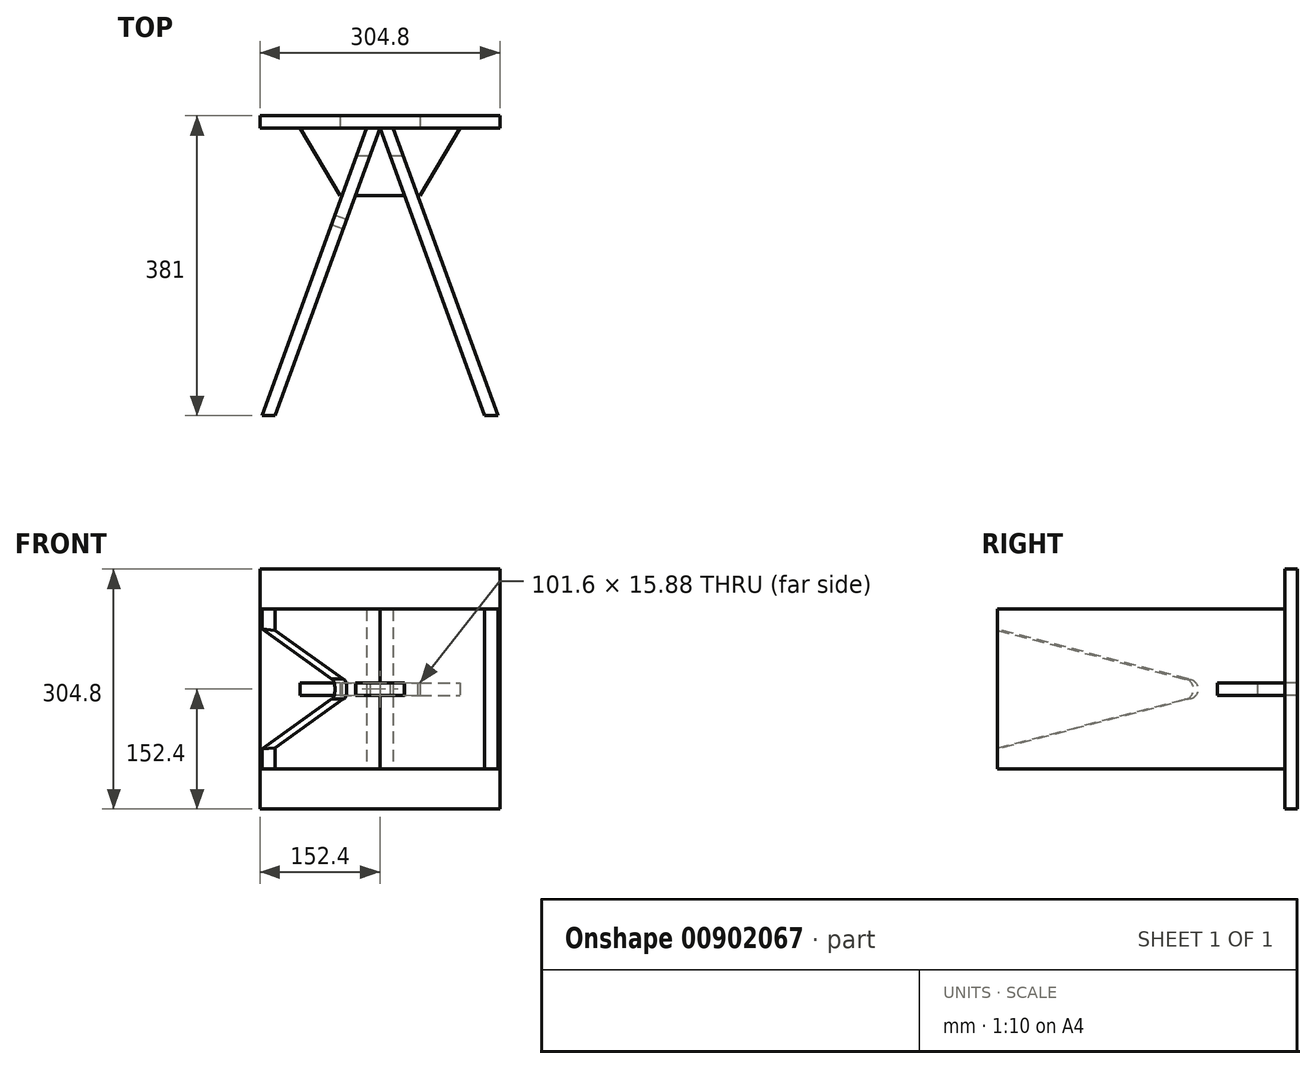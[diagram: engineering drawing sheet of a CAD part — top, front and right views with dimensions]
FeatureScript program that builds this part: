
annotation { "Feature Type Name" : "Feature", "Feature Type Description" : "" }
export const myFeature = defineFeature(function(context is Context, id is Id, definition is map)
    precondition{}
    {
        {
            var Q0;
            Q0=qCreatedBy(makeId("Front.planeOp"),FACE);
            var sketch = newSketch(context, id + "F0", { "sketchPlane" : qUnion([Q0])});
            skLineSegment(sketch, "E0.bottom", {"start": v(152.4, 152.4) * mm, "end": v(-152.4, 152.4) * mm});
            skLineSegment(sketch, "E0.top", {"start": v(152.4, -152.4) * mm, "end": v(-152.4, -152.4) * mm});
            skLineSegment(sketch, "E0.left", {"start": v(152.4, 152.4) * mm, "end": v(152.4, -152.4) * mm});
            skLineSegment(sketch, "E0.right", {"start": v(-152.4, 152.4) * mm, "end": v(-152.4, -152.4) * mm});
            skPoint(sketch, "E0.middle", {"position": v(0, 0) * mm});
            skLineSegment(sketch, "E1.bottom", {"start": v(50.8, 7.94) * mm, "end": v(-50.8, 7.94) * mm});
            skLineSegment(sketch, "E1.top", {"start": v(50.8, -7.94) * mm, "end": v(-50.8, -7.94) * mm});
            skLineSegment(sketch, "E1.left", {"start": v(50.8, 7.94) * mm, "end": v(50.8, -7.94) * mm});
            skLineSegment(sketch, "E1.right", {"start": v(-50.8, 7.94) * mm, "end": v(-50.8, -7.94) * mm});
            skSolve(sketch);
        }
        {
            var Q0;
            Q0=makeQuery(id+"F0.imprint","IMPRINT",FACE,{"disambiguationData":[TD([[makeQuery(id+"F0.imprint","IMPRINT",EDGE,{"derivedFrom":sQuery(id+"F0.wireOp",EDGE,"E0.bottom")}),1.0]])]});
            extrude(context, id + "F1", {"entities" : qUnion([Q0]), "depth" : 15.88 * mm, "offsetDistance" : 25.4 * mm});
        }
        {
            var Q0;
            Q0=qCreatedBy(makeId("Top.planeOp"),FACE);
            var sketch = newSketch(context, id + "F2", { "sketchPlane" : qUnion([Q0])});
            skLineSegment(sketch, "E2.bottom", {"start": v(-50.8, 0) * mm, "end": v(50.8, 0) * mm});
            skLineSegment(sketch, "E2.top", {"start": v(-50.8, -101.6) * mm, "end": v(50.8, -101.6) * mm});
            skLineSegment(sketch, "E2.left", {"start": v(-50.8, 0) * mm, "end": v(-50.8, -101.6) * mm});
            skLineSegment(sketch, "E2.right", {"start": v(50.8, 0) * mm, "end": v(50.8, -101.6) * mm});
            skLineSegment(sketch, "E3.bottom", {"start": v(-50.8, -15.88) * mm, "end": v(-101.6, -15.88) * mm});
            skLineSegment(sketch, "E3.left", {"start": v(-50.8, -15.88) * mm, "end": v(-50.8, -127) * mm});
            skLineSegment(sketch, "E4.bottom", {"start": v(50.8, -15.88) * mm, "end": v(101.6, -15.87) * mm});
            skLineSegment(sketch, "E4.left", {"start": v(50.8, -15.88) * mm, "end": v(50.8, -127) * mm});
            skPoint(sketch, "E5", {"position": v(0, 0) * mm});
            skPoint(sketch, "E6", {"position": v(0, -15.88) * mm});
            skLineSegment(sketch, "E7", {"start": v(0, -15.88) * mm, "end": v(-132.9, -381) * mm});
            skLineSegment(sketch, "E8", {"start": v(-16.9, -15.88) * mm, "end": v(-149.79, -381) * mm});
            skLineSegment(sketch, "E9", {"start": v(-132.9, -381) * mm, "end": v(-149.79, -381) * mm});
            skPoint(sketch, "E10", {"position": v(-149.79, -381) * mm});
            skLineSegment(sketch, "E11", {"start": v(-16.9, -15.88) * mm, "end": v(0, -15.88) * mm});
            skLineSegment(sketch, "E12.MirrorCS", {"start": v(132.9, -381) * mm, "end": v(149.79, -381) * mm});
            skLineSegment(sketch, "E13.MirrorCS", {"start": v(16.9, -15.88) * mm, "end": v(0, -15.88) * mm});
            skLineSegment(sketch, "E14.MirrorCS", {"start": v(16.9, -15.88) * mm, "end": v(149.79, -381) * mm});
            skLineSegment(sketch, "E15.MirrorCS", {"start": v(0, -15.88) * mm, "end": v(132.9, -381) * mm});
            skLineSegment(sketch, "E16", {"start": v(-50.8, -50.8) * mm, "end": v(50.8, -50.8) * mm});
            skLineSegment(sketch, "E17", {"start": v(50.8, -101.6) * mm, "end": v(101.6, -15.87) * mm});
            skLineSegment(sketch, "E18", {"start": v(-50.8, -101.6) * mm, "end": v(-101.6, -15.88) * mm});
            skSolve(sketch);
        }
        {
            var Q0;
            Q0=makeQuery(id+"F2.imprint","IMPRINT",FACE,{"disambiguationData":[TD([[makeQuery(id+"F2.imprint","IMPRINT",EDGE,{"derivedFrom":sQuery(id+"F2.wireOp",EDGE,"E3.bottom")}),1.0]])]});
            var Q1;
            Q1=makeQuery(id+"F2.imprint","IMPRINT",FACE,{"disambiguationData":[TD([[makeQuery(id+"F2.imprint","IMPRINT",EDGE,{"derivedFrom":sQuery(id+"F2.wireOp",EDGE,"E2.bottom")}),-1.0]])]});
            var Q2;
            Q2=makeQuery(id+"F2.imprint","IMPRINT",FACE,{"disambiguationData":[TD([[makeQuery(id+"F2.imprint","IMPRINT",EDGE,{"derivedFrom":sQuery(id+"F2.wireOp",EDGE,"E4.bottom")}),-1.0]])]});
            var Q3;
            {var subQ0=sQuery(id+"F2.wireOp",EDGE,"E7");var subQ1=sQuery(id+"F2.wireOp",EDGE,"E2.top");var subQ2=makeQuery(id+"F2.imprint","INTERSECT",VERTEX,{"derivedFrom":[subQ1,subQ0]});Q3=makeQuery(id+"F2.imprint","IMPRINT",FACE,{"disambiguationData":[TD([[makeQuery(id+"F2.imprint","IMPRINT",EDGE,{"disambiguationData":[TD([[subQ2,-1.0]])],"derivedFrom":subQ1}),1.0]])]});}
            var Q4;
            {var subQ0=sQuery(id+"F2.wireOp",EDGE,"E11");Q4=makeQuery(id+"F2.imprint","IMPRINT",FACE,{"disambiguationData":[TD([[makeQuery(id+"F2.imprint","IMPRINT",EDGE,{"derivedFrom":subQ0}),-1.0]])]});}
            var Q5;
            {var subQ0=sQuery(id+"F2.wireOp",EDGE,"E3.left");var subQ1=sQuery(id+"F2.wireOp",EDGE,"E2.top");var subQ2=makeQuery(id+"F2.imprint","INTERSECT",VERTEX,{"derivedFrom":[subQ1,subQ0]});Q5=makeQuery(id+"F2.imprint","IMPRINT",FACE,{"disambiguationData":[TD([[makeQuery(id+"F2.imprint","IMPRINT",EDGE,{"disambiguationData":[TD([[subQ2,-1.0]])],"derivedFrom":subQ1}),1.0]])]});}
            var Q6;
            {var subQ0=sQuery(id+"F2.wireOp",EDGE,"E13.MirrorCS");Q6=makeQuery(id+"F2.imprint","IMPRINT",FACE,{"disambiguationData":[TD([[makeQuery(id+"F2.imprint","IMPRINT",EDGE,{"derivedFrom":subQ0}),1.0]])]});}
            var Q7;
            {var subQ0=sQuery(id+"F2.wireOp",EDGE,"E4.left");var subQ1=sQuery(id+"F2.wireOp",EDGE,"E2.top");var subQ2=makeQuery(id+"F2.imprint","INTERSECT",VERTEX,{"derivedFrom":[subQ1,subQ0]});Q7=makeQuery(id+"F2.imprint","IMPRINT",FACE,{"disambiguationData":[TD([[makeQuery(id+"F2.imprint","IMPRINT",EDGE,{"disambiguationData":[TD([[subQ2,1.0]])],"derivedFrom":subQ1}),1.0]])]});}
            var Q8;
            {var subQ1=sQuery(id+"F2.wireOp",EDGE,"E7");var subQ3=sQuery(id+"F2.wireOp",EDGE,"E16");var subQ4=makeQuery(id+"F2.imprint","INTERSECT",VERTEX,{"derivedFrom":[subQ1,subQ3]});Q8=makeQuery(id+"F2.imprint","IMPRINT",FACE,{"disambiguationData":[TD([[makeQuery(id+"F2.imprint","IMPRINT",EDGE,{"disambiguationData":[TD([[subQ4,-1.0]])],"derivedFrom":subQ3}),1.0]])]});}
            extrude(context, id + "F3", {"entities" : qUnion([Q0, Q1, Q2, Q3, Q4, Q5, Q6, Q7, Q8]), "depth" : 7.94 * mm, "offsetDistance" : 25.4 * mm, "hasSecondDirection" : true, "secondDirectionOppositeDirection" : true, "secondDirectionDepth" : 7.94 * mm});
        }
        {
            var Q0;
            {var subQ5=sQuery(id+"F2.wireOp",EDGE,"E11");Q0=makeQuery(id+"F2.imprint","IMPRINT",FACE,{"disambiguationData":[TD([[makeQuery(id+"F2.imprint","IMPRINT",EDGE,{"derivedFrom":subQ5}),-1.0]])]});}
            var Q1;
            {var subQ0=sQuery(id+"F2.wireOp",EDGE,"E9");Q1=makeQuery(id+"F2.imprint","IMPRINT",FACE,{"disambiguationData":[TD([[makeQuery(id+"F2.imprint","IMPRINT",EDGE,{"derivedFrom":subQ0}),-1.0]])]});}
            var Q2;
            {var subQ0=sQuery(id+"F2.wireOp",EDGE,"E13.MirrorCS");Q2=makeQuery(id+"F2.imprint","IMPRINT",FACE,{"disambiguationData":[TD([[makeQuery(id+"F2.imprint","IMPRINT",EDGE,{"derivedFrom":subQ0}),1.0]])]});}
            var Q3;
            {var subQ0=sQuery(id+"F2.wireOp",EDGE,"E15.MirrorCS");var subQ1=sQuery(id+"F2.wireOp",EDGE,"E2.top");var subQ2=makeQuery(id+"F2.imprint","INTERSECT",VERTEX,{"derivedFrom":[subQ1,subQ0]});Q3=makeQuery(id+"F2.imprint","IMPRINT",FACE,{"disambiguationData":[TD([[makeQuery(id+"F2.imprint","IMPRINT",EDGE,{"disambiguationData":[TD([[subQ2,-1.0]])],"derivedFrom":subQ1}),1.0]])]});}
            var Q4;
            {var subQ4=sQuery(id+"F2.wireOp",EDGE,"E12.MirrorCS");Q4=makeQuery(id+"F2.imprint","IMPRINT",FACE,{"disambiguationData":[TD([[makeQuery(id+"F2.imprint","IMPRINT",EDGE,{"derivedFrom":subQ4}),1.0]])]});}
            var Q5;
            {var subQ0=sQuery(id+"F2.wireOp",EDGE,"E7");var subQ1=sQuery(id+"F2.wireOp",EDGE,"E2.top");var subQ2=makeQuery(id+"F2.imprint","INTERSECT",VERTEX,{"derivedFrom":[subQ1,subQ0]});Q5=makeQuery(id+"F2.imprint","IMPRINT",FACE,{"disambiguationData":[TD([[makeQuery(id+"F2.imprint","IMPRINT",EDGE,{"disambiguationData":[TD([[subQ2,1.0]])],"derivedFrom":subQ1}),1.0]])]});}
            extrude(context, id + "F4", {"entities" : qUnion([Q0, Q1, Q2, Q3, Q4, Q5]), "depth" : 101.6 * mm, "offsetDistance" : 25.4 * mm, "hasSecondDirection" : true, "secondDirectionOppositeDirection" : true, "secondDirectionDepth" : 101.6 * mm});
        }
        {
            var Q0;
            {var subQ0=sQuery(id+"F2.wireOp",EDGE,"E11");Q0=makeQuery(id+"F2.imprint","IMPRINT",FACE,{"disambiguationData":[TD([[makeQuery(id+"F2.imprint","IMPRINT",EDGE,{"derivedFrom":subQ0}),-1.0]])]});}
            var Q1;
            {var subQ0=sQuery(id+"F2.wireOp",EDGE,"E13.MirrorCS");Q1=makeQuery(id+"F2.imprint","IMPRINT",FACE,{"disambiguationData":[TD([[makeQuery(id+"F2.imprint","IMPRINT",EDGE,{"derivedFrom":subQ0}),1.0]])]});}
            extrude(context, id + "F5", {"entities" : qUnion([Q0, Q1]), "operationType" : NewBodyOperationType.REMOVE, "depth" : 7.94 * mm, "offsetDistance" : 25.4 * mm, "hasSecondDirection" : true, "secondDirectionOppositeDirection" : true, "secondDirectionDepth" : 7.94 * mm});
        }
        {
            var Q0;
            Q0=makeQuery(id+"F4.opExtrude","SWEPT_FACE",FACE,{"disambiguationData":[OSD([sQuery(id+"F2.wireOp",EDGE,"E8")])]});
            var sketch = newSketch(context, id + "F6", { "sketchPlane" : qUnion([Q0])});
            skLineSegment(sketch, "E19", {"start": v(104.95, 0) * mm, "end": v(454.51, 0) * mm, "construction": true});
            skPoint(sketch, "E20.orphan", {"position": v(116.7, 0) * mm});
            skCircle(sketch, "E21", {"center": v(150.95, 0) * mm, "radius": 12.7 * mm});
            skLineSegment(sketch, "E22", {"start": v(150.95, -137.6) * mm, "end": v(150.95, 199.55) * mm, "construction": true});
            skLineSegment(sketch, "E23", {"start": v(150.95, -12.7) * mm, "end": v(409.25, -76.2) * mm});
            skLineSegment(sketch, "E24", {"start": v(150.95, 12.7) * mm, "end": v(409.25, 76.2) * mm});
            skPoint(sketch, "E24.startSnap0", {"position": v(150.95, 30.98) * mm});
            skSolve(sketch);
        }
        {
            var Q0;
            {var subQ0=sQuery(id+"F6.wireOp",EDGE,"E23");Q0=makeQuery(id+"F6.imprint","IMPRINT",FACE,{"disambiguationData":[TD([[makeQuery(id+"F6.imprint","IMPRINT",EDGE,{"derivedFrom":subQ0}),1.0]])]});}
            var Q1;
            {var subQ0=sQuery(id+"F6.wireOp",EDGE,"E21");var subQ1=makeQuery(id+"F6.imprint","INTERSECT",VERTEX,{"derivedFrom":[subQ0,sQuery(id+"F6.wireOp",EDGE,"E23")]});Q1=makeQuery(id+"F6.imprint","IMPRINT",FACE,{"disambiguationData":[TD([[makeQuery(id+"F6.imprint","IMPRINT",EDGE,{"disambiguationData":[TD([[subQ1,1.0]])],"derivedFrom":subQ0}),1.0]])]});}
            extrude(context, id + "F7", {"entities" : qUnion([Q0, Q1]), "operationType" : NewBodyOperationType.REMOVE, "oppositeDirection" : true, "depth" : 25.4 * mm, "offsetDistance" : 25.4 * mm});
        }
    });
